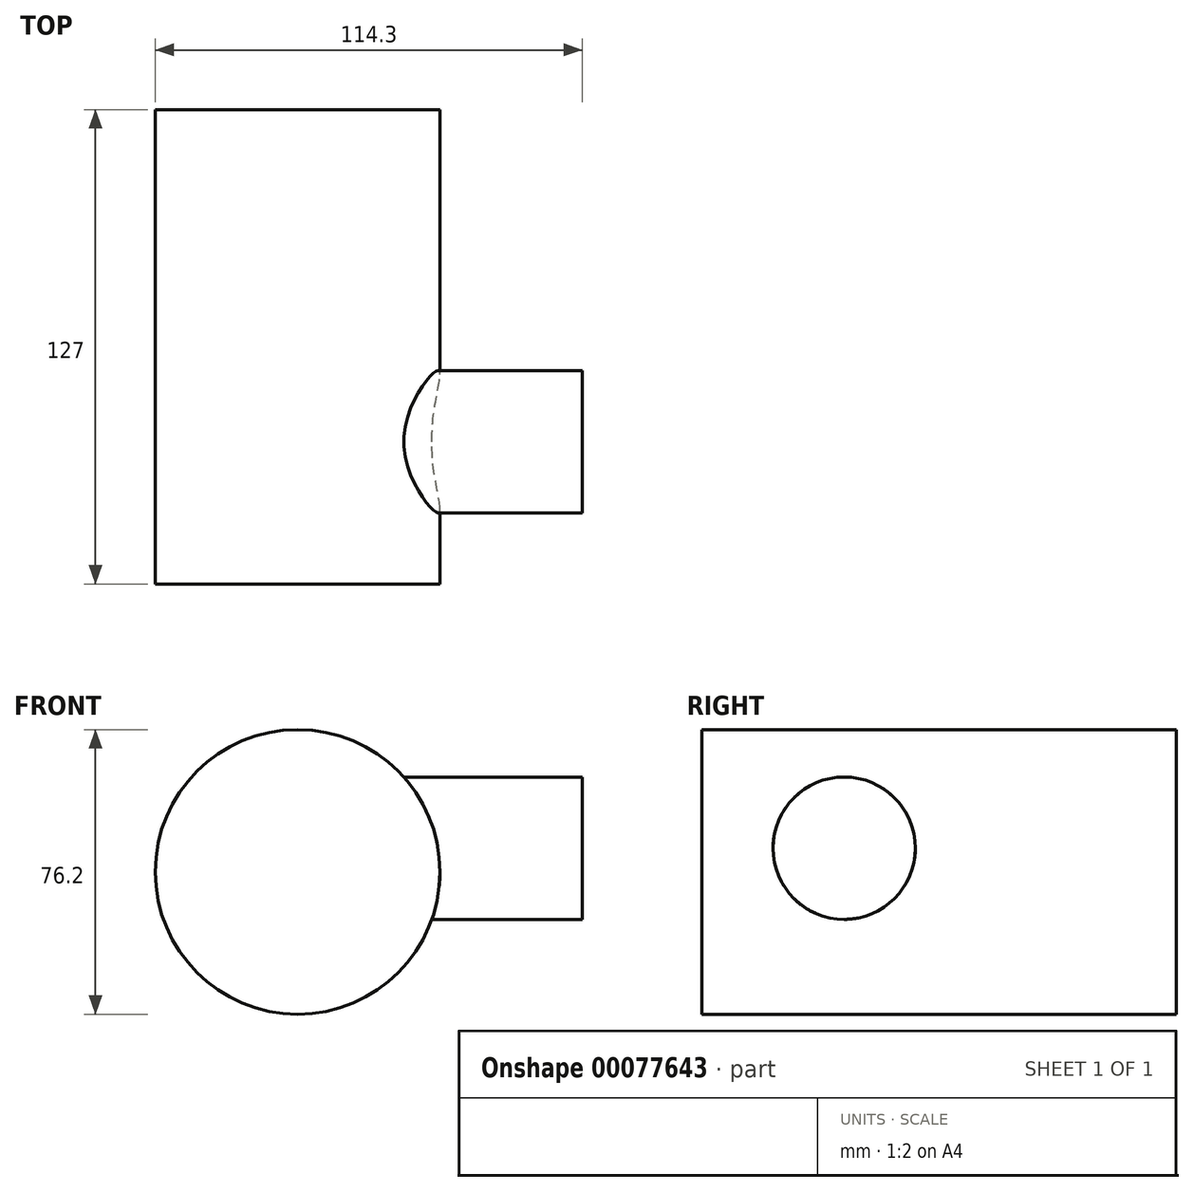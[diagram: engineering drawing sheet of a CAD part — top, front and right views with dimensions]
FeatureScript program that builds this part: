
annotation { "Feature Type Name" : "Feature", "Feature Type Description" : "" }
export const myFeature = defineFeature(function(context is Context, id is Id, definition is map)
    precondition{}
    {
        {
            var Q0;
            Q0=qCreatedBy(makeId("Front.planeOp"),FACE);
            var sketch = newSketch(context, id + "F0", { "sketchPlane" : qUnion([Q0])});
            skCircle(sketch, "E0", {"center": v(0, 0) * mm, "radius": 38.1 * mm});
            skSolve(sketch);
        }
        {
            var Q0;
            Q0=makeQuery(id+"F0.imprint","IMPRINT",FACE,{"disambiguationData":[TD([[makeQuery(id+"F0.imprint","IMPRINT",EDGE,{"derivedFrom":sQuery(id+"F0.wireOp",EDGE,"E0")}),1.0]])]});
            extrude(context, id + "F1", {"entities" : qUnion([Q0]), "endBound" : BoundingType.SYMMETRIC, "depth" : 127 * mm});
        }
        {
            var Q0;
            Q0=qCreatedBy(makeId("Right.planeOp"),FACE);
            cPlane(context, id + "F2", {"entities" : qUnion([Q0]), "cplaneType" : CPlaneType.OFFSET, "offset" : 76.2 * mm, "width" : 152.4 * mm, "height" : 152.4 * mm});
        }
        {
            var Q0;
            Q0=qCreatedBy(id+"F2.planeOp",FACE);
            var sketch = newSketch(context, id + "F3", { "sketchPlane" : qUnion([Q0])});
            skCircle(sketch, "E1", {"center": v(-25.4, 6.35) * mm, "radius": 19.05 * mm});
            skSolve(sketch);
        }
        {
            var Q0;
            Q0=makeQuery(id+"F3.imprint","IMPRINT",FACE,{"disambiguationData":[TD([[makeQuery(id+"F3.imprint","IMPRINT",EDGE,{"derivedFrom":sQuery(id+"F3.wireOp",EDGE,"E1")}),1.0]])]});
            var Q1;
            Q1=makeQuery(id+"F1.opExtrude","SWEPT_BODY",BODY,{"disambiguationData":[OSD([sQuery(id+"F0.wireOp",EDGE,"E0")])]});
            extrude(context, id + "F4", {"entities" : qUnion([Q0]), "operationType" : NewBodyOperationType.ADD, "endBound" : BoundingType.UP_TO_BODY, "oppositeDirection" : true, "endBoundEntityBody" : qUnion([Q1]), "depth" : 25.4 * mm});
        }
    });
